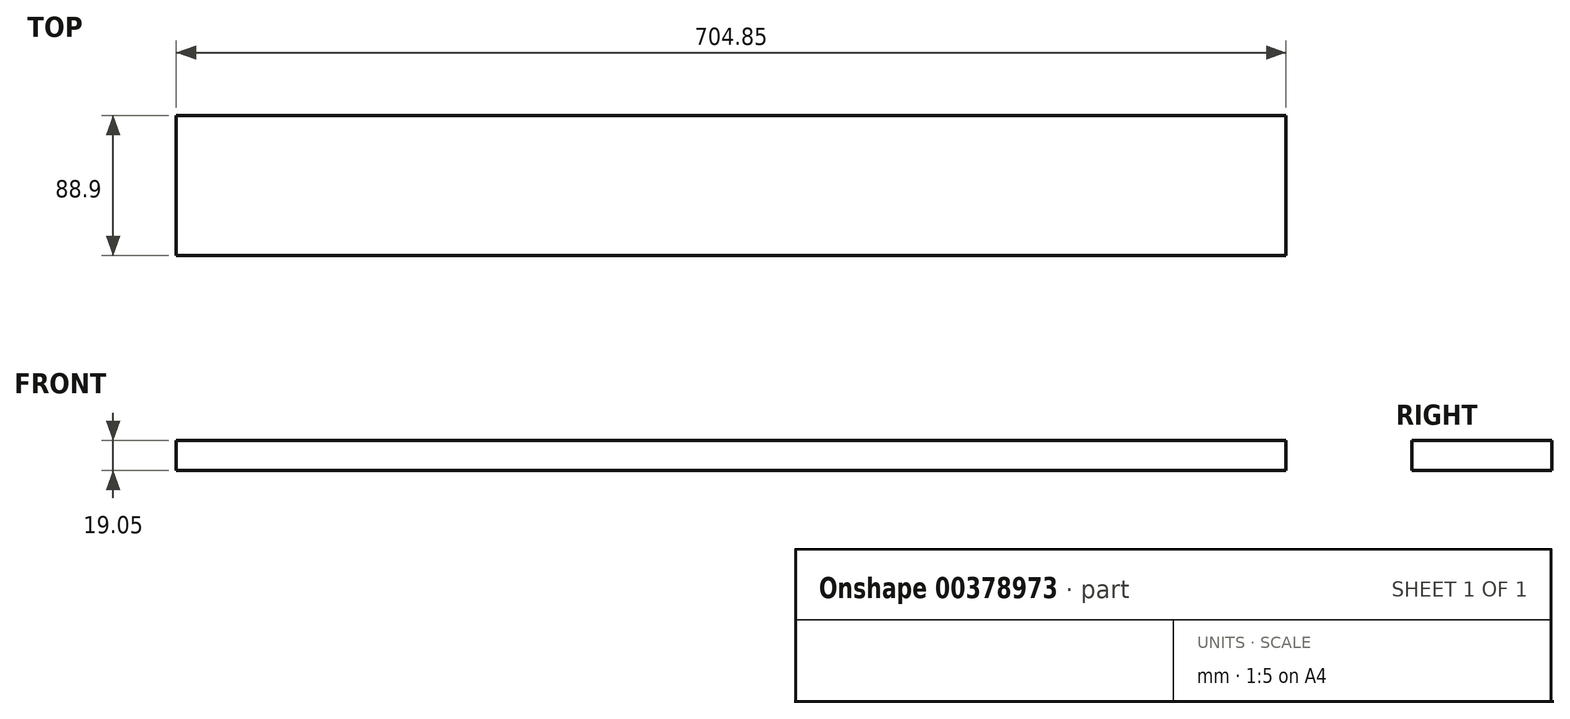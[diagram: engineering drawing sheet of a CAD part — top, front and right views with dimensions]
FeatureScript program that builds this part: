
annotation { "Feature Type Name" : "Feature", "Feature Type Description" : "" }
export const myFeature = defineFeature(function(context is Context, id is Id, definition is map)
    precondition{}
    {
        {
            var Q0;
            Q0=qCreatedBy(makeId("Top.planeOp"),FACE);
            var sketch = newSketch(context, id + "F0", { "sketchPlane" : qUnion([Q0])});
            skLineSegment(sketch, "E0.bottom", {"start": v(-66.37, 39.77) * mm, "end": v(638.48, 39.77) * mm});
            skLineSegment(sketch, "E0.top", {"start": v(-66.37, -49.13) * mm, "end": v(638.48, -49.13) * mm});
            skLineSegment(sketch, "E0.left", {"start": v(-66.37, 39.77) * mm, "end": v(-66.37, -49.13) * mm});
            skLineSegment(sketch, "E0.right", {"start": v(638.48, 39.77) * mm, "end": v(638.48, -49.13) * mm});
            skSolve(sketch);
        }
        {
            var Q0;
            Q0=makeQuery(id+"F0.imprint","IMPRINT",FACE,{"disambiguationData":[TD([[makeQuery(id+"F0.imprint","IMPRINT",EDGE,{"derivedFrom":sQuery(id+"F0.wireOp",EDGE,"E0.bottom")}),-1.0]])]});
            extrude(context, id + "F1", {"entities" : qUnion([Q0]), "depth" : 19.05 * mm, "offsetDistance" : 25.4 * mm});
        }
    });
